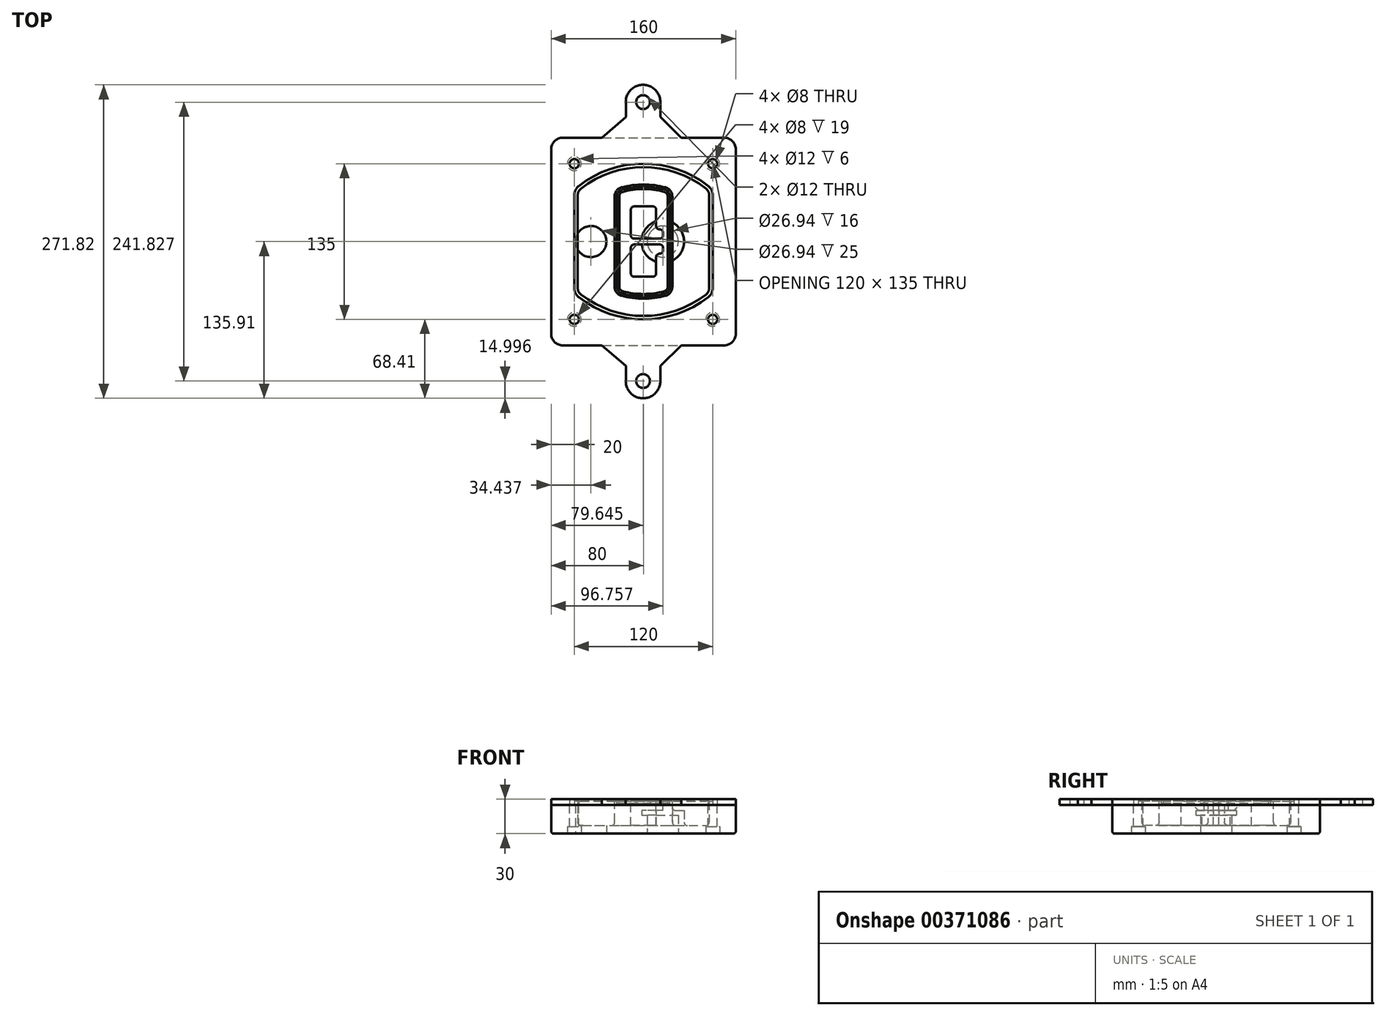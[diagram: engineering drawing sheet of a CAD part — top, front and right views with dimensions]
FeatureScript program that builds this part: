
annotation { "Feature Type Name" : "Feature", "Feature Type Description" : "" }
export const myFeature = defineFeature(function(context is Context, id is Id, definition is map)
    precondition{}
    {
        {
            var Q0;
            Q0=qCreatedBy(makeId("Top.planeOp"),FACE);
            var sketch = newSketch(context, id + "F0", { "sketchPlane" : qUnion([Q0])});
            skPoint(sketch, "E0.rect.middle", {"position": v(0, 0) * mm});
            skLineSegment(sketch, "E1.bottom", {"start": v(-70, -90) * mm, "end": v(70, -90) * mm});
            skLineSegment(sketch, "E1.top", {"start": v(-70, 90) * mm, "end": v(70, 90) * mm});
            skLineSegment(sketch, "E1.left", {"start": v(-80, -80) * mm, "end": v(-80, 80) * mm});
            skLineSegment(sketch, "E1.right", {"start": v(80, -80) * mm, "end": v(80, 80) * mm});
            skLineSegment(sketch, "E2", {"start": v(-80, 90) * mm, "end": v(80, -90) * mm, "construction": true});
            skLineSegment(sketch, "E3", {"start": v(80, 90) * mm, "end": v(-80, -90) * mm, "construction": true});
            skCircle(sketch, "E4", {"center": v(-60, 67.5) * mm, "radius": 4 * mm});
            skCircle(sketch, "E5", {"center": v(60, 67.5) * mm, "radius": 4 * mm});
            skCircle(sketch, "E6", {"center": v(60, -67.5) * mm, "radius": 4 * mm});
            skCircle(sketch, "E7", {"center": v(-60, -67.5) * mm, "radius": 4 * mm});
            skLineSegment(sketch, "E8", {"start": v(-60, 67.5) * mm, "end": v(60, 67.5) * mm, "construction": true});
            skLineSegment(sketch, "E9", {"start": v(60, 67.5) * mm, "end": v(60, -67.5) * mm, "construction": true});
            skLineSegment(sketch, "E10", {"start": v(60, -67.5) * mm, "end": v(-60, -67.5) * mm, "construction": true});
            skLineSegment(sketch, "E11", {"start": v(-60, -67.5) * mm, "end": v(-60, 67.5) * mm, "construction": true});
            skLineSegment(sketch, "E12", {"start": v(-60, 40.3) * mm, "end": v(-60, -40.3) * mm});
            skLineSegment(sketch, "E13", {"start": v(60, 40.3) * mm, "end": v(60, -40.3) * mm});
            skArc(sketch, "E14", {"start": v(56.15, 48.18) * mm, "mid": v(0, 67.5) * mm, "end": v(-56.15, 48.18) * mm});
            skArc(sketch, "E15", {"start": v(-56.15, -48.18) * mm, "mid": v(0, -67.5) * mm, "end": v(56.15, -48.18) * mm});
            skLineSegment(sketch, "E16", {"start": v(-60, 0) * mm, "end": v(60, 0) * mm, "construction": true});
            skPoint(sketch, "E17.visualSharp", {"position": v(-60, -45) * mm});
            skArc(sketch, "E17.filletArc", {"start": v(-60, -40.3) * mm, "mid": v(-58.99, -44.68) * mm, "end": v(-56.15, -48.18) * mm});
            skPoint(sketch, "E18.visualSharp", {"position": v(-60, 45) * mm});
            skArc(sketch, "E18.filletArc", {"start": v(-56.15, 48.18) * mm, "mid": v(-58.99, 44.68) * mm, "end": v(-60, 40.3) * mm});
            skPoint(sketch, "E19.visualSharp", {"position": v(60, 45) * mm});
            skArc(sketch, "E19.filletArc", {"start": v(60, 40.3) * mm, "mid": v(58.99, 44.68) * mm, "end": v(56.15, 48.18) * mm});
            skPoint(sketch, "E20.visualSharp", {"position": v(60, -45) * mm});
            skArc(sketch, "E20.filletArc", {"start": v(56.15, -48.18) * mm, "mid": v(58.99, -44.68) * mm, "end": v(60, -40.3) * mm});
            skPoint(sketch, "E21.visualSharp", {"position": v(-80, 90) * mm});
            skArc(sketch, "E21.filletArc", {"start": v(-70, 90) * mm, "mid": v(-77.07, 87.07) * mm, "end": v(-80, 80) * mm});
            skPoint(sketch, "E22.visualSharp", {"position": v(80, 90) * mm});
            skArc(sketch, "E22.filletArc", {"start": v(80, 80) * mm, "mid": v(77.07, 87.07) * mm, "end": v(70, 90) * mm});
            skPoint(sketch, "E23.visualSharp", {"position": v(80, -90) * mm});
            skArc(sketch, "E23.filletArc", {"start": v(70, -90) * mm, "mid": v(77.07, -87.07) * mm, "end": v(80, -80) * mm});
            skPoint(sketch, "E24.visualSharp", {"position": v(-80, -90) * mm});
            skArc(sketch, "E24.filletArc", {"start": v(-80, -80) * mm, "mid": v(-77.07, -87.07) * mm, "end": v(-70, -90) * mm});
            skArc(sketch, "E25.0", {"start": v(57, 40.3) * mm, "mid": v(56.3, 43.36) * mm, "end": v(54.3, 45.81) * mm});
            skLineSegment(sketch, "E25.1", {"start": v(57, 40.3) * mm, "end": v(57, -40.3) * mm});
            skArc(sketch, "E25.2", {"start": v(54.3, -45.81) * mm, "mid": v(56.3, -43.36) * mm, "end": v(57, -40.3) * mm});
            skArc(sketch, "E25.3", {"start": v(-54.3, -45.81) * mm, "mid": v(0, -64.5) * mm, "end": v(54.3, -45.81) * mm});
            skArc(sketch, "E25.4", {"start": v(-57, -40.3) * mm, "mid": v(-56.3, -43.36) * mm, "end": v(-54.3, -45.81) * mm});
            skArc(sketch, "E25.5", {"start": v(54.3, 45.81) * mm, "mid": v(0, 64.5) * mm, "end": v(-54.3, 45.81) * mm});
            skLineSegment(sketch, "E25.6", {"start": v(-57, 40.3) * mm, "end": v(-57, -40.3) * mm});
            skArc(sketch, "E25.7", {"start": v(-54.3, 45.81) * mm, "mid": v(-56.3, 43.36) * mm, "end": v(-57, 40.3) * mm});
            skArc(sketch, "E26.0", {"start": v(-58.62, 51.33) * mm, "mid": v(-62.58, 46.43) * mm, "end": v(-64, 40.3) * mm});
            skArc(sketch, "E26.1", {"start": v(58.62, 51.33) * mm, "mid": v(0, 71.5) * mm, "end": v(-58.62, 51.33) * mm});
            skArc(sketch, "E26.2", {"start": v(64, 40.3) * mm, "mid": v(62.58, 46.43) * mm, "end": v(58.62, 51.33) * mm});
            skLineSegment(sketch, "E26.3", {"start": v(64, 40.3) * mm, "end": v(64, -40.3) * mm});
            skArc(sketch, "E26.4", {"start": v(58.62, -51.33) * mm, "mid": v(62.58, -46.43) * mm, "end": v(64, -40.3) * mm});
            skLineSegment(sketch, "E26.5", {"start": v(-64, 40.3) * mm, "end": v(-64, -40.3) * mm});
            skArc(sketch, "E26.6", {"start": v(-58.62, -51.33) * mm, "mid": v(0, -71.5) * mm, "end": v(58.62, -51.33) * mm});
            skArc(sketch, "E26.7", {"start": v(-64, -40.3) * mm, "mid": v(-62.58, -46.43) * mm, "end": v(-58.62, -51.33) * mm});
            skSolve(sketch);
        }
        {
            var Q0;
            Q0=makeQuery(id+"F0.imprint","IMPRINT",FACE,{"disambiguationData":[TD([[makeQuery(id+"F0.imprint","IMPRINT",EDGE,{"derivedFrom":sQuery(id+"F0.wireOp",EDGE,"E1.bottom")}),1.0]])]});
            var Q1;
            Q1=makeQuery(id+"F0.imprint","IMPRINT",FACE,{"disambiguationData":[TD([[makeQuery(id+"F0.imprint","IMPRINT",EDGE,{"derivedFrom":sQuery(id+"F0.wireOp",EDGE,"E12")}),1.0]])]});
            var Q2;
            Q2=makeQuery(id+"F0.imprint","IMPRINT",FACE,{"disambiguationData":[TD([[makeQuery(id+"F0.imprint","IMPRINT",EDGE,{"derivedFrom":sQuery(id+"F0.wireOp",EDGE,"E25.0")}),1.0]])]});
            var Q3;
            Q3=makeQuery(id+"F0.imprint","IMPRINT",FACE,{"disambiguationData":[TD([[makeQuery(id+"F0.imprint","IMPRINT",EDGE,{"derivedFrom":sQuery(id+"F0.wireOp",EDGE,"E12")}),-1.0]])]});
            extrude(context, id + "F1", {"entities" : qUnion([Q0, Q1, Q2, Q3]), "oppositeDirection" : true, "depth" : 25 * mm});
        }
        {
            var Q0;
            Q0=makeQuery(id+"F0.imprint","IMPRINT",FACE,{"disambiguationData":[TD([[makeQuery(id+"F0.imprint","IMPRINT",EDGE,{"derivedFrom":sQuery(id+"F0.wireOp",EDGE,"E12")}),1.0]])]});
            extrude(context, id + "F2", {"entities" : qUnion([Q0]), "operationType" : NewBodyOperationType.ADD, "depth" : 3 * mm});
        }
        {
            var Q0;
            Q0=makeQuery(id+"F0.imprint","IMPRINT",FACE,{"disambiguationData":[TD([[makeQuery(id+"F0.imprint","IMPRINT",EDGE,{"derivedFrom":sQuery(id+"F0.wireOp",EDGE,"E25.0")}),1.0]])]});
            extrude(context, id + "F3", {"entities" : qUnion([Q0]), "operationType" : NewBodyOperationType.REMOVE, "oppositeDirection" : true, "depth" : 18 * mm});
        }
        {
            var Q0;
            Q0=makeQuery(id+"F2.opExtrude","CAP_FACE",FACE,{"disambiguationData":[OSD([sQuery(id+"F0.wireOp",EDGE,"E12"),sQuery(id+"F0.wireOp",EDGE,"E13"),sQuery(id+"F0.wireOp",EDGE,"E14"),sQuery(id+"F0.wireOp",EDGE,"E15"),sQuery(id+"F0.wireOp",EDGE,"E17.filletArc"),sQuery(id+"F0.wireOp",EDGE,"E18.filletArc"),sQuery(id+"F0.wireOp",EDGE,"E19.filletArc"),sQuery(id+"F0.wireOp",EDGE,"E20.filletArc"),sQuery(id+"F0.wireOp",EDGE,"E25.0"),sQuery(id+"F0.wireOp",EDGE,"E25.1"),sQuery(id+"F0.wireOp",EDGE,"E25.2"),sQuery(id+"F0.wireOp",EDGE,"E25.3"),sQuery(id+"F0.wireOp",EDGE,"E25.4"),sQuery(id+"F0.wireOp",EDGE,"E25.5"),sQuery(id+"F0.wireOp",EDGE,"E25.6"),sQuery(id+"F0.wireOp",EDGE,"E25.7")])],"isStart":false});
            var sketch = newSketch(context, id + "F4", { "sketchPlane" : qUnion([Q0])});
            skArc(sketch, "E27.0", {"start": v(-19.08, -46.97) * mm, "mid": v(0, -49.5) * mm, "end": v(19.08, -46.97) * mm});
            skArc(sketch, "E28.0", {"start": v(19.08, 46.97) * mm, "mid": v(0, 49.5) * mm, "end": v(-19.08, 46.97) * mm});
            skLineSegment(sketch, "E29", {"start": v(-25, 39.25) * mm, "end": v(-25, -39.25) * mm});
            skLineSegment(sketch, "E30", {"start": v(25, 39.25) * mm, "end": v(25, -39.25) * mm});
            skLineSegment(sketch, "E31", {"start": v(-25, 45.1) * mm, "end": v(25, 45.1) * mm, "construction": true});
            skLineSegment(sketch, "E32", {"start": v(-25, -45.1) * mm, "end": v(25, -45.1) * mm, "construction": true});
            skPoint(sketch, "E33.visualSharp", {"position": v(-25, 45.1) * mm});
            skArc(sketch, "E33.filletArc", {"start": v(-19.08, 46.97) * mm, "mid": v(-23.35, 44.11) * mm, "end": v(-25, 39.25) * mm});
            skPoint(sketch, "E34.visualSharp", {"position": v(25, 45.1) * mm});
            skArc(sketch, "E34.filletArc", {"start": v(25, 39.25) * mm, "mid": v(23.35, 44.11) * mm, "end": v(19.08, 46.97) * mm});
            skPoint(sketch, "E35.visualSharp", {"position": v(25, -45.1) * mm});
            skArc(sketch, "E35.filletArc", {"start": v(19.08, -46.97) * mm, "mid": v(23.35, -44.11) * mm, "end": v(25, -39.25) * mm});
            skPoint(sketch, "E36.visualSharp", {"position": v(-25, -45.1) * mm});
            skArc(sketch, "E36.filletArc", {"start": v(-25, -39.25) * mm, "mid": v(-23.35, -44.11) * mm, "end": v(-19.08, -46.97) * mm});
            skArc(sketch, "E37.0", {"start": v(54.3, 45.81) * mm, "mid": v(0, 64.5) * mm, "end": v(-54.3, 45.81) * mm});
            skArc(sketch, "E37.1", {"start": v(-54.3, 45.81) * mm, "mid": v(-56.3, 43.36) * mm, "end": v(-57, 40.3) * mm});
            skLineSegment(sketch, "E37.2", {"start": v(-57, 40.3) * mm, "end": v(-57, -40.3) * mm});
            skArc(sketch, "E37.3", {"start": v(-57, -40.3) * mm, "mid": v(-56.3, -43.36) * mm, "end": v(-54.3, -45.81) * mm});
            skArc(sketch, "E37.4", {"start": v(-54.3, -45.81) * mm, "mid": v(0, -64.5) * mm, "end": v(54.3, -45.81) * mm});
            skArc(sketch, "E37.5", {"start": v(54.3, -45.81) * mm, "mid": v(56.3, -43.36) * mm, "end": v(57, -40.3) * mm});
            skLineSegment(sketch, "E37.6", {"start": v(57, 40.3) * mm, "end": v(57, -40.3) * mm});
            skArc(sketch, "E37.7", {"start": v(57, 40.3) * mm, "mid": v(56.3, 43.36) * mm, "end": v(54.3, 45.81) * mm});
            skLineSegment(sketch, "E38.0", {"start": v(23, 39.25) * mm, "end": v(23, -39.25) * mm});
            skArc(sketch, "E38.1", {"start": v(18.56, -45.04) * mm, "mid": v(21.76, -42.9) * mm, "end": v(23, -39.25) * mm});
            skArc(sketch, "E38.2", {"start": v(-18.56, -45.04) * mm, "mid": v(0, -47.5) * mm, "end": v(18.56, -45.04) * mm});
            skArc(sketch, "E38.3", {"start": v(-23, -39.25) * mm, "mid": v(-21.76, -42.9) * mm, "end": v(-18.56, -45.04) * mm});
            skLineSegment(sketch, "E38.4", {"start": v(-23, 39.25) * mm, "end": v(-23, -39.25) * mm});
            skArc(sketch, "E38.5", {"start": v(23, 39.25) * mm, "mid": v(21.76, 42.9) * mm, "end": v(18.56, 45.04) * mm});
            skArc(sketch, "E38.6", {"start": v(-18.56, 45.04) * mm, "mid": v(-21.76, 42.9) * mm, "end": v(-23, 39.25) * mm});
            skArc(sketch, "E38.7", {"start": v(18.56, 45.04) * mm, "mid": v(0, 47.5) * mm, "end": v(-18.56, 45.04) * mm});
            skArc(sketch, "E39.0", {"start": v(21, 39.25) * mm, "mid": v(20.18, 41.68) * mm, "end": v(18.04, 43.1) * mm});
            skLineSegment(sketch, "E39.1", {"start": v(21, 39.25) * mm, "end": v(21, -39.25) * mm});
            skArc(sketch, "E39.2", {"start": v(18.04, -43.1) * mm, "mid": v(20.18, -41.68) * mm, "end": v(21, -39.25) * mm});
            skArc(sketch, "E39.3", {"start": v(-18.04, -43.1) * mm, "mid": v(0, -45.5) * mm, "end": v(18.04, -43.1) * mm});
            skArc(sketch, "E39.4", {"start": v(-21, -39.25) * mm, "mid": v(-20.18, -41.68) * mm, "end": v(-18.04, -43.1) * mm});
            skArc(sketch, "E39.5", {"start": v(18.04, 43.1) * mm, "mid": v(0, 45.5) * mm, "end": v(-18.04, 43.1) * mm});
            skLineSegment(sketch, "E39.6", {"start": v(-21, 39.25) * mm, "end": v(-21, -39.25) * mm});
            skArc(sketch, "E39.7", {"start": v(-18.04, 43.1) * mm, "mid": v(-20.18, 41.68) * mm, "end": v(-21, 39.25) * mm});
            skLineSegment(sketch, "E40", {"start": v(-25, 0) * mm, "end": v(25, 0) * mm, "construction": true});
            skLineSegment(sketch, "E41", {"start": v(-11, 5.5) * mm, "end": v(-11, 27.5) * mm});
            skLineSegment(sketch, "E42", {"start": v(-8, 30.5) * mm, "end": v(8, 30.5) * mm});
            skLineSegment(sketch, "E43", {"start": v(11, 27.5) * mm, "end": v(11, 13.5) * mm});
            skLineSegment(sketch, "E44", {"start": v(14, 10.5) * mm, "end": v(14, 10.5) * mm});
            skLineSegment(sketch, "E45", {"start": v(17, 7.5) * mm, "end": v(17, 5.5) * mm});
            skLineSegment(sketch, "E46", {"start": v(14, 2.5) * mm, "end": v(-8, 2.5) * mm});
            skPoint(sketch, "E47.visualSharp", {"position": v(-11, 30.5) * mm});
            skArc(sketch, "E47.filletArc", {"start": v(-8, 30.5) * mm, "mid": v(-10.12, 29.62) * mm, "end": v(-11, 27.5) * mm});
            skPoint(sketch, "E48.visualSharp", {"position": v(11, 30.5) * mm});
            skArc(sketch, "E48.filletArc", {"start": v(11, 27.5) * mm, "mid": v(10.12, 29.62) * mm, "end": v(8, 30.5) * mm});
            skPoint(sketch, "E49.visualSharp", {"position": v(11, 10.5) * mm});
            skArc(sketch, "E49.filletArc", {"start": v(11, 13.5) * mm, "mid": v(11.88, 11.38) * mm, "end": v(14, 10.5) * mm});
            skPoint(sketch, "E50.visualSharp", {"position": v(17, 10.5) * mm});
            skArc(sketch, "E50.filletArc", {"start": v(17, 7.5) * mm, "mid": v(16.12, 9.62) * mm, "end": v(14, 10.5) * mm});
            skPoint(sketch, "E51.visualSharp", {"position": v(17, 2.5) * mm});
            skArc(sketch, "E51.filletArc", {"start": v(14, 2.5) * mm, "mid": v(16.12, 3.38) * mm, "end": v(17, 5.5) * mm});
            skPoint(sketch, "E52.visualSharp", {"position": v(-11, 2.5) * mm});
            skArc(sketch, "E52.filletArc", {"start": v(-11, 5.5) * mm, "mid": v(-10.12, 3.38) * mm, "end": v(-8, 2.5) * mm});
            skLineSegment(sketch, "E53.0.MirrorCS", {"start": v(14, -2.5) * mm, "end": v(-8, -2.5) * mm});
            skArc(sketch, "E54.0.MirrorCS", {"start": v(-11, -5.5) * mm, "mid": v(-10.12, -3.38) * mm, "end": v(-8, -2.5) * mm});
            skLineSegment(sketch, "E55.0.MirrorCS", {"start": v(-11, -5.5) * mm, "end": v(-11, -27.5) * mm});
            skArc(sketch, "E56.0.MirrorCS", {"start": v(-8, -30.5) * mm, "mid": v(-10.12, -29.62) * mm, "end": v(-11, -27.5) * mm});
            skLineSegment(sketch, "E57.0.MirrorCS", {"start": v(-8, -30.5) * mm, "end": v(8, -30.5) * mm});
            skArc(sketch, "E58.0.MirrorCS", {"start": v(11, -27.5) * mm, "mid": v(10.12, -29.62) * mm, "end": v(8, -30.5) * mm});
            skLineSegment(sketch, "E59.0.MirrorCS", {"start": v(11, -27.5) * mm, "end": v(11, -13.5) * mm});
            skArc(sketch, "E60.0.MirrorCS", {"start": v(11, -13.5) * mm, "mid": v(11.88, -11.38) * mm, "end": v(14, -10.5) * mm});
            skArc(sketch, "E61.0.MirrorCS", {"start": v(17, -7.5) * mm, "mid": v(16.12, -9.62) * mm, "end": v(14, -10.5) * mm});
            skLineSegment(sketch, "E62.0.MirrorCS", {"start": v(17, -7.5) * mm, "end": v(17, -5.5) * mm});
            skArc(sketch, "E63.0.MirrorCS", {"start": v(14, -2.5) * mm, "mid": v(16.12, -3.38) * mm, "end": v(17, -5.5) * mm});
            skSolve(sketch);
        }
        {
            var Q0;
            Q0=makeQuery(id+"F4.imprint","IMPRINT",FACE,{"disambiguationData":[TD([[makeQuery(id+"F4.imprint","IMPRINT",EDGE,{"derivedFrom":sQuery(id+"F4.wireOp",EDGE,"E27.0")}),1.0]])]});
            var Q1;
            Q1=makeQuery(id+"F4.imprint","IMPRINT",FACE,{"disambiguationData":[TD([[makeQuery(id+"F4.imprint","IMPRINT",EDGE,{"derivedFrom":sQuery(id+"F4.wireOp",EDGE,"E38.0")}),-1.0]])]});
            var Q2;
            Q2=makeQuery(id+"F4.imprint","IMPRINT",FACE,{"disambiguationData":[TD([[makeQuery(id+"F4.imprint","IMPRINT",EDGE,{"derivedFrom":sQuery(id+"F4.wireOp",EDGE,"E39.0")}),1.0]])]});
            extrude(context, id + "F5", {"entities" : qUnion([Q0, Q1, Q2]), "operationType" : NewBodyOperationType.ADD, "endBound" : BoundingType.UP_TO_NEXT, "oppositeDirection" : true, "depth" : 25 * mm});
        }
        {
            var Q0;
            Q0=makeQuery(id+"F4.imprint","IMPRINT",FACE,{"disambiguationData":[TD([[makeQuery(id+"F4.imprint","IMPRINT",EDGE,{"derivedFrom":sQuery(id+"F4.wireOp",EDGE,"E38.0")}),-1.0]])]});
            extrude(context, id + "F6", {"entities" : qUnion([Q0]), "operationType" : NewBodyOperationType.REMOVE, "oppositeDirection" : true, "depth" : 2 * mm});
        }
        {
            var Q0;
            Q0=makeQuery(id+"F1.opExtrude","CAP_FACE",FACE,{"disambiguationData":[OSD([sQuery(id+"F0.wireOp",EDGE,"E1.bottom"),sQuery(id+"F0.wireOp",EDGE,"E1.top"),sQuery(id+"F0.wireOp",EDGE,"E1.left"),sQuery(id+"F0.wireOp",EDGE,"E1.right"),sQuery(id+"F0.wireOp",EDGE,"E4"),sQuery(id+"F0.wireOp",EDGE,"E5"),sQuery(id+"F0.wireOp",EDGE,"E6"),sQuery(id+"F0.wireOp",EDGE,"E7"),sQuery(id+"F0.wireOp",EDGE,"E21.filletArc"),sQuery(id+"F0.wireOp",EDGE,"E22.filletArc"),sQuery(id+"F0.wireOp",EDGE,"E23.filletArc"),sQuery(id+"F0.wireOp",EDGE,"E24.filletArc")])],"isStart":false});
            var sketch = newSketch(context, id + "F7", { "sketchPlane" : qUnion([Q0])});
            skCircle(sketch, "E64", {"center": v(16.76, 0) * mm, "radius": 13.47 * mm});
            skCircle(sketch, "E65", {"center": v(-45.56, 0) * mm, "radius": 13.47 * mm});
            skLineSegment(sketch, "E66", {"start": v(80, 0) * mm, "end": v(-80, 0) * mm});
            skCircle(sketch, "E67", {"center": v(16.76, 0) * mm, "radius": 18.47 * mm});
            skCircle(sketch, "E68", {"center": v(60, -67.5) * mm, "radius": 6 * mm});
            skCircle(sketch, "E69", {"center": v(-60, -67.5) * mm, "radius": 6 * mm});
            skCircle(sketch, "E70", {"center": v(-60, 67.5) * mm, "radius": 6 * mm});
            skCircle(sketch, "E71", {"center": v(60, 67.5) * mm, "radius": 6 * mm});
            skSolve(sketch);
        }
        {
            var Q0;
            {var subQ1=sQuery(id+"F7.wireOp",EDGE,"E66");var subQ4=sQuery(id+"F7.wireOp",EDGE,"E64");var subQ6=makeQuery(id+"F7.imprint","INTERSECT",VERTEX,{"disambiguationData":[OD(0.0)],"derivedFrom":[subQ4,subQ1]});Q0=makeQuery(id+"F7.imprint","IMPRINT",FACE,{"disambiguationData":[TD([[makeQuery(id+"F7.imprint","IMPRINT",EDGE,{"disambiguationData":[TD([[subQ6,-1.0]])],"derivedFrom":subQ4}),-1.0]])]});}
            var Q1;
            {var subQ0=sQuery(id+"F7.wireOp",EDGE,"E66");var subQ1=sQuery(id+"F7.wireOp",EDGE,"E64");var subQ3=makeQuery(id+"F7.imprint","INTERSECT",VERTEX,{"disambiguationData":[OD(0.0)],"derivedFrom":[subQ1,subQ0]});Q1=makeQuery(id+"F7.imprint","IMPRINT",FACE,{"disambiguationData":[TD([[makeQuery(id+"F7.imprint","IMPRINT",EDGE,{"disambiguationData":[TD([[subQ3,-1.0]])],"derivedFrom":subQ1}),1.0]])]});}
            var Q2;
            {var subQ0=sQuery(id+"F7.wireOp",EDGE,"E66");var subQ1=sQuery(id+"F7.wireOp",EDGE,"E64");var subQ3=makeQuery(id+"F7.imprint","INTERSECT",VERTEX,{"disambiguationData":[OD(0.0)],"derivedFrom":[subQ1,subQ0]});Q2=makeQuery(id+"F7.imprint","IMPRINT",FACE,{"disambiguationData":[TD([[makeQuery(id+"F7.imprint","IMPRINT",EDGE,{"disambiguationData":[TD([[subQ3,1.0]])],"derivedFrom":subQ1}),1.0]])]});}
            var Q3;
            {var subQ1=sQuery(id+"F7.wireOp",EDGE,"E66");var subQ4=sQuery(id+"F7.wireOp",EDGE,"E64");var subQ6=makeQuery(id+"F7.imprint","INTERSECT",VERTEX,{"disambiguationData":[OD(0.0)],"derivedFrom":[subQ4,subQ1]});Q3=makeQuery(id+"F7.imprint","IMPRINT",FACE,{"disambiguationData":[TD([[makeQuery(id+"F7.imprint","IMPRINT",EDGE,{"disambiguationData":[TD([[subQ6,1.0]])],"derivedFrom":subQ4}),-1.0]])]});}
            extrude(context, id + "F8", {"entities" : qUnion([Q0, Q1, Q2, Q3]), "operationType" : NewBodyOperationType.ADD, "oppositeDirection" : true, "depth" : 20 * mm});
        }
        {
            var Q0;
            {var subQ0=sQuery(id+"F7.wireOp",EDGE,"E66");var subQ1=sQuery(id+"F7.wireOp",EDGE,"E64");var subQ3=makeQuery(id+"F7.imprint","INTERSECT",VERTEX,{"disambiguationData":[OD(0.0)],"derivedFrom":[subQ1,subQ0]});Q0=makeQuery(id+"F7.imprint","IMPRINT",FACE,{"disambiguationData":[TD([[makeQuery(id+"F7.imprint","IMPRINT",EDGE,{"disambiguationData":[TD([[subQ3,-1.0]])],"derivedFrom":subQ1}),1.0]])]});}
            var Q1;
            {var subQ0=sQuery(id+"F7.wireOp",EDGE,"E66");var subQ1=sQuery(id+"F7.wireOp",EDGE,"E64");var subQ3=makeQuery(id+"F7.imprint","INTERSECT",VERTEX,{"disambiguationData":[OD(0.0)],"derivedFrom":[subQ1,subQ0]});Q1=makeQuery(id+"F7.imprint","IMPRINT",FACE,{"disambiguationData":[TD([[makeQuery(id+"F7.imprint","IMPRINT",EDGE,{"disambiguationData":[TD([[subQ3,1.0]])],"derivedFrom":subQ1}),1.0]])]});}
            extrude(context, id + "F9", {"entities" : qUnion([Q0, Q1]), "operationType" : NewBodyOperationType.REMOVE, "oppositeDirection" : true, "depth" : 16 * mm});
        }
        {
            var Q0;
            {var subQ0=sQuery(id+"F7.wireOp",EDGE,"E66");var subQ1=sQuery(id+"F7.wireOp",EDGE,"E65");var subQ3=makeQuery(id+"F7.imprint","INTERSECT",VERTEX,{"disambiguationData":[OD(0.0)],"derivedFrom":[subQ1,subQ0]});Q0=makeQuery(id+"F7.imprint","IMPRINT",FACE,{"disambiguationData":[TD([[makeQuery(id+"F7.imprint","IMPRINT",EDGE,{"disambiguationData":[TD([[subQ3,-1.0]])],"derivedFrom":subQ1}),1.0]])]});}
            var Q1;
            {var subQ0=sQuery(id+"F7.wireOp",EDGE,"E66");var subQ1=sQuery(id+"F7.wireOp",EDGE,"E65");var subQ3=makeQuery(id+"F7.imprint","INTERSECT",VERTEX,{"disambiguationData":[OD(0.0)],"derivedFrom":[subQ1,subQ0]});Q1=makeQuery(id+"F7.imprint","IMPRINT",FACE,{"disambiguationData":[TD([[makeQuery(id+"F7.imprint","IMPRINT",EDGE,{"disambiguationData":[TD([[subQ3,1.0]])],"derivedFrom":subQ1}),1.0]])]});}
            extrude(context, id + "F10", {"entities" : qUnion([Q0, Q1]), "operationType" : NewBodyOperationType.REMOVE, "oppositeDirection" : true, "depth" : 25 * mm});
        }
        {
            var Q0;
            Q0=makeQuery(id+"F7.imprint","IMPRINT",FACE,{"disambiguationData":[TD([[makeQuery(id+"F7.imprint","IMPRINT",EDGE,{"derivedFrom":sQuery(id+"F7.wireOp",EDGE,"E68")}),1.0]])]});
            var Q1;
            Q1=makeQuery(id+"F7.imprint","IMPRINT",FACE,{"disambiguationData":[TD([[makeQuery(id+"F7.imprint","IMPRINT",EDGE,{"derivedFrom":makeQuery(id+"F1.opExtrude","CAP_EDGE",EDGE,{"disambiguationData":[OSD([sQuery(id+"F0.wireOp",EDGE,"E5")])],"isStart":false})}),-1.0]])]});
            var Q2;
            Q2=makeQuery(id+"F7.imprint","IMPRINT",FACE,{"disambiguationData":[TD([[makeQuery(id+"F7.imprint","IMPRINT",EDGE,{"derivedFrom":sQuery(id+"F7.wireOp",EDGE,"E69")}),1.0]])]});
            var Q3;
            Q3=makeQuery(id+"F7.imprint","IMPRINT",FACE,{"disambiguationData":[TD([[makeQuery(id+"F7.imprint","IMPRINT",EDGE,{"derivedFrom":makeQuery(id+"F1.opExtrude","CAP_EDGE",EDGE,{"disambiguationData":[OSD([sQuery(id+"F0.wireOp",EDGE,"E4")])],"isStart":false})}),-1.0]])]});
            var Q4;
            Q4=makeQuery(id+"F7.imprint","IMPRINT",FACE,{"disambiguationData":[TD([[makeQuery(id+"F7.imprint","IMPRINT",EDGE,{"derivedFrom":sQuery(id+"F7.wireOp",EDGE,"E70")}),1.0]])]});
            var Q5;
            Q5=makeQuery(id+"F7.imprint","IMPRINT",FACE,{"disambiguationData":[TD([[makeQuery(id+"F7.imprint","IMPRINT",EDGE,{"derivedFrom":makeQuery(id+"F1.opExtrude","CAP_EDGE",EDGE,{"disambiguationData":[OSD([sQuery(id+"F0.wireOp",EDGE,"E7")])],"isStart":false})}),-1.0]])]});
            var Q6;
            Q6=makeQuery(id+"F7.imprint","IMPRINT",FACE,{"disambiguationData":[TD([[makeQuery(id+"F7.imprint","IMPRINT",EDGE,{"derivedFrom":sQuery(id+"F7.wireOp",EDGE,"E71")}),1.0]])]});
            var Q7;
            Q7=makeQuery(id+"F7.imprint","IMPRINT",FACE,{"disambiguationData":[TD([[makeQuery(id+"F7.imprint","IMPRINT",EDGE,{"derivedFrom":makeQuery(id+"F1.opExtrude","CAP_EDGE",EDGE,{"disambiguationData":[OSD([sQuery(id+"F0.wireOp",EDGE,"E6")])],"isStart":false})}),-1.0]])]});
            extrude(context, id + "F11", {"entities" : qUnion([Q0, Q1, Q2, Q3, Q4, Q5, Q6, Q7]), "operationType" : NewBodyOperationType.REMOVE, "oppositeDirection" : true, "depth" : 6 * mm});
        }
        {
            var Q0;
            Q0=makeQuery(id+"F9.boolean.opBoolean","COPY",FACE,{"derivedFrom":makeQuery(id+"F9.opExtrude","CAP_FACE",FACE,{"disambiguationData":[OSD([sQuery(id+"F7.wireOp",EDGE,"E64")])],"isStart":false})});
            var sketch = newSketch(context, id + "F12", { "sketchPlane" : qUnion([Q0])});
            skArc(sketch, "E72.0", {"start": v(11, 17.55) * mm, "mid": v(2.57, 11.82) * mm, "end": v(-1.54, 2.5) * mm});
            skArc(sketch, "E72.1", {"start": v(-1.54, -2.5) * mm, "mid": v(2.57, -11.82) * mm, "end": v(11, -17.55) * mm});
            skLineSegment(sketch, "E73", {"start": v(-1.54, -2.5) * mm, "end": v(14, -2.5) * mm});
            skLineSegment(sketch, "E74.0", {"start": v(14, 2.5) * mm, "end": v(-1.54, 2.5) * mm});
            skArc(sketch, "E74.1", {"start": v(14, 2.5) * mm, "mid": v(16.12, 3.38) * mm, "end": v(17, 5.5) * mm});
            skLineSegment(sketch, "E74.2", {"start": v(17, 7.5) * mm, "end": v(17, 5.5) * mm});
            skArc(sketch, "E74.3", {"start": v(17, 7.5) * mm, "mid": v(16.12, 9.62) * mm, "end": v(14, 10.5) * mm});
            skArc(sketch, "E74.4", {"start": v(11, 13.5) * mm, "mid": v(11.88, 11.38) * mm, "end": v(14, 10.5) * mm});
            skLineSegment(sketch, "E74.5", {"start": v(11, 17.55) * mm, "end": v(11, 13.5) * mm});
            skLineSegment(sketch, "E74.7", {"start": v(14, -2.5) * mm, "end": v(-1.54, -2.5) * mm});
            skArc(sketch, "E74.8", {"start": v(14, -2.5) * mm, "mid": v(16.12, -3.38) * mm, "end": v(17, -5.5) * mm});
            skLineSegment(sketch, "E74.9", {"start": v(17, -7.5) * mm, "end": v(17, -5.5) * mm});
            skArc(sketch, "E74.10", {"start": v(17, -7.5) * mm, "mid": v(16.12, -9.62) * mm, "end": v(14, -10.5) * mm});
            skArc(sketch, "E74.11", {"start": v(11, -13.5) * mm, "mid": v(11.88, -11.38) * mm, "end": v(14, -10.5) * mm});
            skLineSegment(sketch, "E74.12", {"start": v(11, -17.55) * mm, "end": v(11, -13.5) * mm});
            skPoint(sketch, "E75.orphan", {"position": v(11, -27.5) * mm});
            skPoint(sketch, "E76.orphan", {"position": v(-8, -2.5) * mm});
            skPoint(sketch, "E77.orphan", {"position": v(-8, 2.5) * mm});
            skPoint(sketch, "E78.orphan", {"position": v(11, 27.5) * mm});
            skSolve(sketch);
        }
        {
            var Q0;
            {var subQ7=sQuery(id+"F12.wireOp",EDGE,"E72.0");var subQ14=sQuery(id+"F12.wireOp",EDGE,"E72.1");var subQ16=sQuery(id+"F12.wireOp",EDGE,"E74.1");var subQ18=sQuery(id+"F12.wireOp",EDGE,"E74.8");Q0=qUnion([makeQuery(id+"F12.imprint","IMPRINT",FACE,{"disambiguationData":[TD([[makeQuery(id+"F12.imprint","IMPRINT",EDGE,{"derivedFrom":subQ7}),1.0]])]}),makeQuery(id+"F12.imprint","IMPRINT",FACE,{"disambiguationData":[TD([[makeQuery(id+"F12.imprint","IMPRINT",EDGE,{"derivedFrom":subQ14}),1.0]])]}),makeQuery(id+"F12.imprint","IMPRINT",FACE,{"disambiguationData":[TD([[makeQuery(id+"F12.imprint","IMPRINT",EDGE,{"derivedFrom":subQ16}),1.0]])]}),makeQuery(id+"F12.imprint","IMPRINT",FACE,{"disambiguationData":[TD([[makeQuery(id+"F12.imprint","IMPRINT",EDGE,{"derivedFrom":subQ18}),-1.0]])]})]);}
            var Q1;
            Q1=makeQuery(id+"F5.boolean.opBoolean","SPLIT",FACE,{"disambiguationData":[TD([makeQuery(id+"F5.opExtrude","SWEPT_FACE",FACE,{"disambiguationData":[OSD([sQuery(id+"F4.wireOp",EDGE,"E41")])]})])],"derivedFrom":makeQuery(id+"F3.boolean.opBoolean","COPY",FACE,{"derivedFrom":makeQuery(id+"F3.opExtrude","CAP_FACE",FACE,{"disambiguationData":[OSD([sQuery(id+"F0.wireOp",EDGE,"E25.0"),sQuery(id+"F0.wireOp",EDGE,"E25.1"),sQuery(id+"F0.wireOp",EDGE,"E25.2"),sQuery(id+"F0.wireOp",EDGE,"E25.3"),sQuery(id+"F0.wireOp",EDGE,"E25.4"),sQuery(id+"F0.wireOp",EDGE,"E25.5"),sQuery(id+"F0.wireOp",EDGE,"E25.6"),sQuery(id+"F0.wireOp",EDGE,"E25.7")])],"isStart":false})})});
            extrude(context, id + "F13", {"entities" : qUnion([Q0]), "operationType" : NewBodyOperationType.REMOVE, "endBound" : BoundingType.UP_TO_SURFACE, "endBoundEntityFace" : qUnion([Q1]), "depth" : 25 * mm});
        }
        {
            var Q0;
            Q0=makeQuery(id+"F3.boolean.opBoolean","COPY",EDGE,{"derivedFrom":makeQuery(id+"F3.opExtrude","CAP_EDGE",EDGE,{"disambiguationData":[OSD([sQuery(id+"F0.wireOp",EDGE,"E25.6")])],"isStart":false})});
            var Q1;
            Q1=makeQuery(id+"F8.boolean.opBoolean","INTERSECT",EDGE,{"derivedFrom":[makeQuery(id+"F5.opExtrude","SWEPT_FACE",FACE,{"disambiguationData":[OSD([sQuery(id+"F4.wireOp",EDGE,"E30")])]}),makeQuery(id+"F8.opExtrude","CAP_FACE",FACE,{"disambiguationData":[OSD([sQuery(id+"F7.wireOp",EDGE,"E67")])],"isStart":false})]});
            var Q2;
            Q2=makeQuery(id+"F8.boolean.opBoolean","INTERSECT",EDGE,{"disambiguationData":[OD(1.0)],"derivedFrom":[makeQuery(id+"F5.opExtrude","SWEPT_FACE",FACE,{"disambiguationData":[OSD([sQuery(id+"F4.wireOp",EDGE,"E30")])]}),makeQuery(id+"F8.opExtrude","SWEPT_FACE",FACE,{"disambiguationData":[OSD([sQuery(id+"F7.wireOp",EDGE,"E67")])]})]});
            var Q3;
            {var subQ0=sQuery(id+"F4.wireOp",EDGE,"E30");Q3=makeQuery(id+"F8.boolean.opBoolean","SPLIT",EDGE,{"disambiguationData":[TD([makeQuery(id+"F5.opExtrude","SWEPT_FACE",FACE,{"disambiguationData":[OSD([sQuery(id+"F4.wireOp",EDGE,"E35.filletArc")])]})])],"derivedFrom":makeQuery(id+"F5.opExtrude","CAP_EDGE",EDGE,{"disambiguationData":[OSD([subQ0])],"isStart":false})});}
            var Q4;
            {var subQ0=sQuery(id+"F0.wireOp",EDGE,"E25.7");var subQ1=sQuery(id+"F0.wireOp",EDGE,"E25.1");var subQ2=sQuery(id+"F0.wireOp",EDGE,"E25.6");var subQ3=sQuery(id+"F0.wireOp",EDGE,"E25.5");var subQ4=sQuery(id+"F0.wireOp",EDGE,"E25.4");var subQ5=sQuery(id+"F0.wireOp",EDGE,"E25.0");var subQ6=sQuery(id+"F0.wireOp",EDGE,"E25.2");var subQ7=sQuery(id+"F0.wireOp",EDGE,"E25.3");Q4=makeQuery(id+"F8.boolean.opBoolean","INTERSECT",EDGE,{"derivedFrom":[makeQuery(id+"F5.boolean.opBoolean","SPLIT",FACE,{"disambiguationData":[TD([makeQuery(id+"F2.opExtrude","SWEPT_FACE",FACE,{"disambiguationData":[OSD([subQ5])]})])],"derivedFrom":makeQuery(id+"F3.boolean.opBoolean","COPY",FACE,{"derivedFrom":makeQuery(id+"F3.opExtrude","CAP_FACE",FACE,{"disambiguationData":[OSD([subQ5,subQ1,subQ6,subQ7,subQ4,subQ3,subQ2,subQ0])],"isStart":false})})}),makeQuery(id+"F8.opExtrude","SWEPT_FACE",FACE,{"disambiguationData":[OSD([sQuery(id+"F7.wireOp",EDGE,"E67")])]})]});}
            var Q5;
            Q5=makeQuery(id+"F8.boolean.opBoolean","INTERSECT",EDGE,{"disambiguationData":[OD(0.0)],"derivedFrom":[makeQuery(id+"F5.opExtrude","SWEPT_FACE",FACE,{"disambiguationData":[OSD([sQuery(id+"F4.wireOp",EDGE,"E30")])]}),makeQuery(id+"F8.opExtrude","SWEPT_FACE",FACE,{"disambiguationData":[OSD([sQuery(id+"F7.wireOp",EDGE,"E67")])]})]});
            fillet(context, id + "F14", {"entities" : qUnion([Q0, Q1, Q2, Q3, Q4, Q5]), "radius" : 3 * mm, "tangentPropagation" : true, "allowEdgeOverflow" : false});
        }
        {
            var Q0;
            Q0=makeQuery(id+"F1.opExtrude","CAP_EDGE",EDGE,{"disambiguationData":[OSD([sQuery(id+"F0.wireOp",EDGE,"E1.bottom")])],"isStart":false});
            fillet(context, id + "F15", {"entities" : qUnion([Q0]), "radius" : 2 * mm, "tangentPropagation" : true, "allowEdgeOverflow" : false});
        }
        {
            var Q0;
            {var subQ0=sQuery(id+"F0.wireOp",EDGE,"E21.filletArc");var subQ1=sQuery(id+"F0.wireOp",EDGE,"E7");var subQ2=sQuery(id+"F0.wireOp",EDGE,"E6");var subQ3=sQuery(id+"F0.wireOp",EDGE,"E5");var subQ4=sQuery(id+"F0.wireOp",EDGE,"E4");var subQ5=sQuery(id+"F0.wireOp",EDGE,"E22.filletArc");var subQ6=sQuery(id+"F0.wireOp",EDGE,"E1.bottom");var subQ7=sQuery(id+"F0.wireOp",EDGE,"E1.right");var subQ8=sQuery(id+"F0.wireOp",EDGE,"E1.top");var subQ9=sQuery(id+"F0.wireOp",EDGE,"E1.left");var subQ10=sQuery(id+"F0.wireOp",EDGE,"E23.filletArc");var subQ11=sQuery(id+"F0.wireOp",EDGE,"E24.filletArc");Q0=makeQuery(id+"F2.boolean.opBoolean","SPLIT",FACE,{"disambiguationData":[TD([makeQuery(id+"F1.opExtrude","SWEPT_FACE",FACE,{"disambiguationData":[OSD([subQ6])]})])],"derivedFrom":makeQuery(id+"F1.opExtrude","CAP_FACE",FACE,{"disambiguationData":[OSD([subQ6,subQ8,subQ9,subQ7,subQ4,subQ3,subQ2,subQ1,subQ0,subQ5,subQ10,subQ11])],"isStart":true})});}
            var sketch = newSketch(context, id + "F16", { "sketchPlane" : qUnion([Q0])});
            skArc(sketch, "E79", {"start": v(14.62, 120) * mm, "mid": v(-0.36, 135.91) * mm, "end": v(-15.33, 120) * mm});
            skCircle(sketch, "E80", {"center": v(-0.36, 120.91) * mm, "radius": 6 * mm});
            skLineSegment(sketch, "E81", {"start": v(-15.33, 120) * mm, "end": v(-15.33, 108) * mm});
            skLineSegment(sketch, "E82", {"start": v(-15.33, 108) * mm, "end": v(-36.04, 90) * mm});
            skLineSegment(sketch, "E83", {"start": v(14.62, 120) * mm, "end": v(14.62, 108) * mm});
            skLineSegment(sketch, "E84", {"start": v(14.62, 108) * mm, "end": v(32.62, 90) * mm});
            skLineSegment(sketch, "E85", {"start": v(-0.36, 120.91) * mm, "end": v(-0.36, 90) * mm, "construction": true});
            skLineSegment(sketch, "E86", {"start": v(94.54, 0) * mm, "end": v(-97.6, 0) * mm, "construction": true});
            skPoint(sketch, "E86.endSnap0", {"position": v(-80, 0) * mm});
            skLineSegment(sketch, "E87.MirrorCS", {"start": v(-15.33, -120) * mm, "end": v(-15.33, -108) * mm});
            skLineSegment(sketch, "E88.MirrorCS", {"start": v(14.62, -120) * mm, "end": v(14.62, -108) * mm});
            skCircle(sketch, "E89.MirrorC", {"center": v(-0.36, -120.91) * mm, "radius": 6 * mm});
            skLineSegment(sketch, "E90.MirrorCS", {"start": v(-15.33, -108) * mm, "end": v(-36.04, -90) * mm});
            skLineSegment(sketch, "E91.MirrorCS", {"start": v(14.62, -108) * mm, "end": v(32.62, -90) * mm});
            skLineSegment(sketch, "E92.MirrorCS", {"start": v(-0.36, -120.91) * mm, "end": v(-0.36, -90) * mm, "construction": true});
            skArc(sketch, "E93.MirrorCS", {"start": v(14.62, -120) * mm, "mid": v(-0.36, -135.91) * mm, "end": v(-15.33, -120) * mm});
            skSolve(sketch);
        }
        {
            var Q0;
            Q0=makeQuery(id+"F16.imprint","IMPRINT",FACE,{"disambiguationData":[TD([[makeQuery(id+"F16.imprint","IMPRINT",EDGE,{"derivedFrom":sQuery(id+"F16.wireOp",EDGE,"E79")}),1.0]])]});
            var Q1;
            Q1=makeQuery(id+"F16.imprint","IMPRINT",FACE,{"disambiguationData":[TD([[makeQuery(id+"F16.imprint","IMPRINT",EDGE,{"derivedFrom":makeQuery(id+"F1.opExtrude","CAP_EDGE",EDGE,{"disambiguationData":[OSD([sQuery(id+"F0.wireOp",EDGE,"E1.left")])],"isStart":true})}),-1.0]])]});
            var Q2;
            Q2=makeQuery(id+"F16.imprint","IMPRINT",FACE,{"disambiguationData":[TD([[makeQuery(id+"F16.imprint","IMPRINT",EDGE,{"derivedFrom":sQuery(id+"F16.wireOp",EDGE,"E87.MirrorCS")}),-1.0]])]});
            extrude(context, id + "F17", {"entities" : qUnion([Q0, Q1, Q2]), "depth" : 5 * mm});
        }
    });
